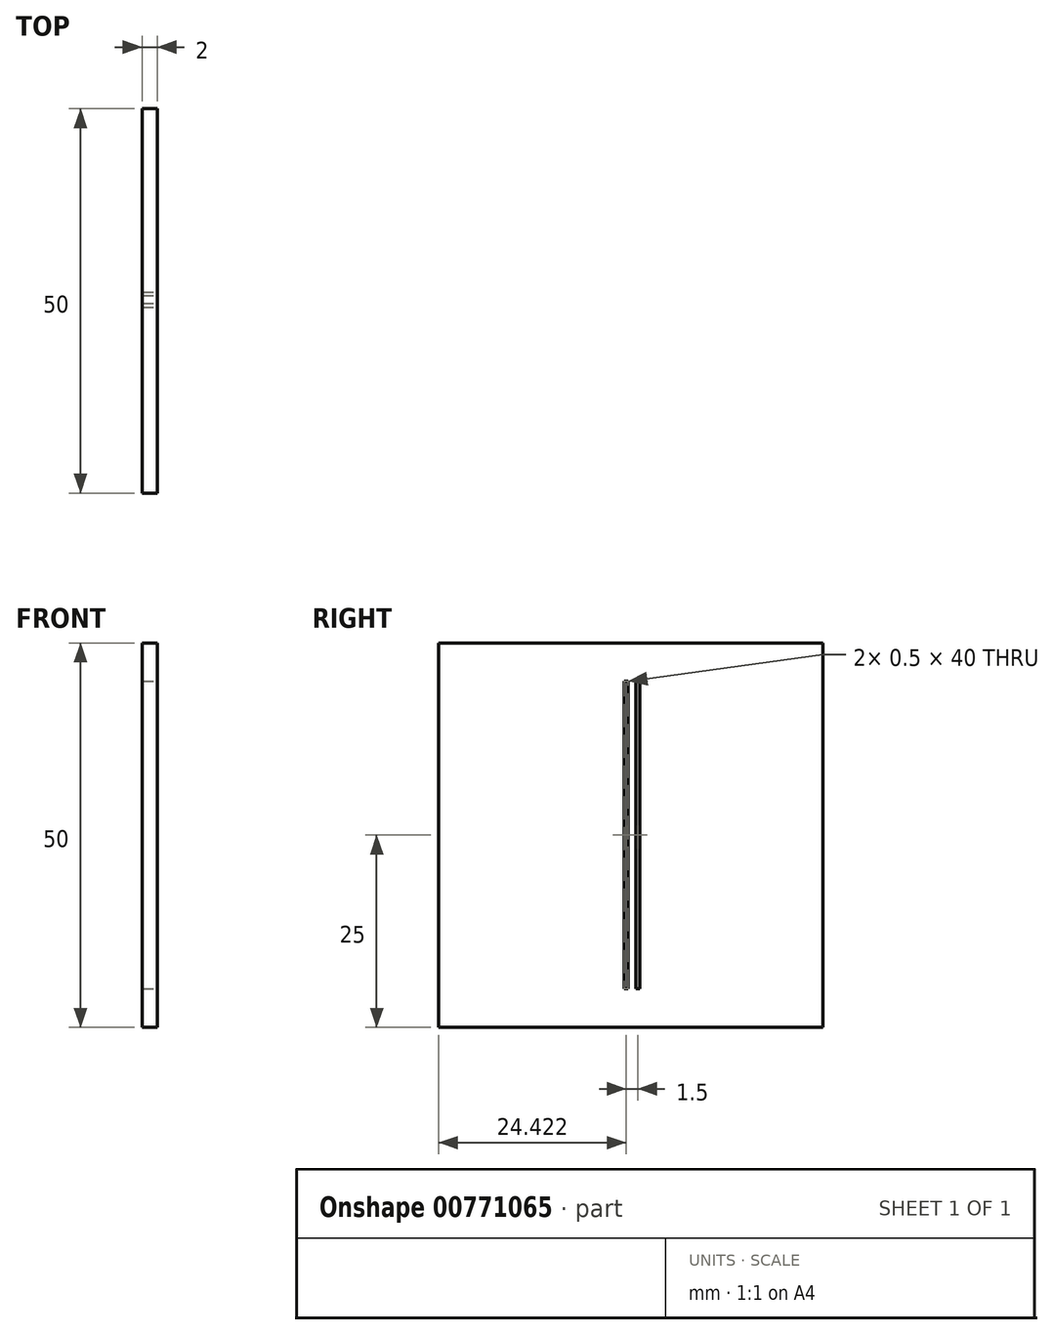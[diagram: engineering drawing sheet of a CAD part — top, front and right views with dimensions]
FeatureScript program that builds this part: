
annotation { "Feature Type Name" : "Feature", "Feature Type Description" : "" }
export const myFeature = defineFeature(function(context is Context, id is Id, definition is map)
    precondition{}
    {
        {
            var Q0;
            Q0=qCreatedBy(makeId("Right.planeOp"),FACE);
            var sketch = newSketch(context, id + "F0", { "sketchPlane" : qUnion([Q0])});
            skLineSegment(sketch, "E0.bottom", {"start": v(-25, -25) * mm, "end": v(25, -25) * mm});
            skLineSegment(sketch, "E0.top", {"start": v(-25, 25) * mm, "end": v(25, 25) * mm});
            skLineSegment(sketch, "E0.left", {"start": v(-25, -25) * mm, "end": v(-25, 25) * mm});
            skLineSegment(sketch, "E0.right", {"start": v(25, -25) * mm, "end": v(25, 25) * mm});
            skPoint(sketch, "E0.middle", {"position": v(0, 0) * mm});
            skSolve(sketch);
        }
        {
            var Q0;
            Q0 = qSketchRegion(id + "F0", true);
            extrude(context, id + "F1", {"entities" : qUnion([Q0]), "depth" : 2 * mm, "offsetDistance" : 25 * mm});
        }
        {
            var Q0;
            Q0=makeQuery(id+"F1.opExtrude","CAP_FACE",FACE,{"disambiguationData":[OSD([sQuery(id+"F0.wireOp",EDGE,"E0.bottom"),sQuery(id+"F0.wireOp",EDGE,"E0.top"),sQuery(id+"F0.wireOp",EDGE,"E0.left"),sQuery(id+"F0.wireOp",EDGE,"E0.right")])],"isStart":false});
            var sketch = newSketch(context, id + "F2", { "sketchPlane" : qUnion([Q0])});
            skLineSegment(sketch, "E1.bottom", {"start": v(-0.83, 20) * mm, "end": v(-0.33, 20) * mm});
            skLineSegment(sketch, "E1.top", {"start": v(-0.83, -20) * mm, "end": v(-0.33, -20) * mm});
            skLineSegment(sketch, "E1.left", {"start": v(-0.83, 20) * mm, "end": v(-0.83, -20) * mm});
            skLineSegment(sketch, "E1.right", {"start": v(-0.33, 20) * mm, "end": v(-0.33, -20) * mm});
            skLineSegment(sketch, "E2.bottom", {"start": v(0.67, 20) * mm, "end": v(1.17, 20) * mm});
            skLineSegment(sketch, "E2.top", {"start": v(0.67, -20) * mm, "end": v(1.17, -20) * mm});
            skLineSegment(sketch, "E2.left", {"start": v(0.67, 20) * mm, "end": v(0.67, -20) * mm});
            skLineSegment(sketch, "E2.right", {"start": v(1.17, 20) * mm, "end": v(1.17, -20) * mm});
            skSolve(sketch);
        }
        {
            var Q0;
            Q0 = qSketchRegion(id + "F2", true);
            extrude(context, id + "F3", {"entities" : qUnion([Q0]), "operationType" : NewBodyOperationType.REMOVE, "endBound" : BoundingType.THROUGH_ALL, "oppositeDirection" : true, "depth" : 25 * mm, "offsetDistance" : 25 * mm});
        }
    });
